# Revit family: P300316-009
name_source: partatom
category: Lighting Fixtures
revit_build: Autodesk Revit 2014 (Build: 20130308_1515(x64)
units: mm (PartAtom-declared; Revit-internal decimal feet)

## types (1)
- P300317-009
    Apparent Load = 100 VA
    Assembly Code = D5020200
    Connector Description = Lighting Connector
    Default Elevation = 48 "
    Description = Ashford Collection Four-Light Brushed Nickel and Opal Glass Farmhouse Style Bath Vanity Wall Light
    Features = Provide nostalgic charm with the Ashford Collection 4-Light Brushed Nickel Opal Glass Farmhouse Bath Vanity Light. The circular backplate, elegantly curved arms, and vintage light bases are coated in a beautiful brushed nickel finish for a crisp aesthetic. Light sources glow from inside opal glass shades that skillfully blend the old with the new.
Application: Provide nostalgic charm with the Ashford Collection 4-Light Brushed Nickel Opal Glass Farmhouse Bath Vanity Light ideal for any bathroom.
Styles: Perfect for farmhouse, coastal, and transitional style settings.
Finish: The circular backplate, elegantly curved arms, and vintage light bases are coated in a beautiful brushed nickel finish for a crisp aesthetic.
Materials: Constructed from steel to ensure a long product lifespan. Mount the light fixture facing up or down.
Glass/Shade: Light sources glow from inside opal glass shades that skillfully blend the old with the new.
Bulbs: For ideal illumination, use 4 medium base bulbs that are sold separately (100w max - LED/CFL/incandescent). Compatible with dimmable bulbs.
Dimensions: Measures 33-1/2-inch width by 10-inch height by 8-inch depth.
Certifications: cULus damp location listed.
Pairs With: Pairs with a variety of Progress Lighting fixtures.
Warranty: Our 1-Year Limited Warranty guarantees your complete satisfaction with your purchase and includes professional after-sales customer service support.
    Fixture distribution = Direct
    Glass = Hubbell - White Glass
    Gold = Hubbell - Gold
    Housing Material = Paint - Hubbell - Metallic Silver Textured
    Lamp = Incandescent
    Load Classification = Lighting
    Manufacturer = Progress Lighting
    Model = P300317-009
    Power Factor = 1
    Product Documentation Link = https://hubbellcdn.com
    Product Link = https://www.hubbell.com
    URL = https://www.hubbell.com
    Voltage = 120 V
    Warranty = 1 year Warranty
    Wattage Comments = 100W
    Watts = 100 W

## geometry (parser evidence)
native form markers: Sweep x7
no freeform markers — native parametric forms only
